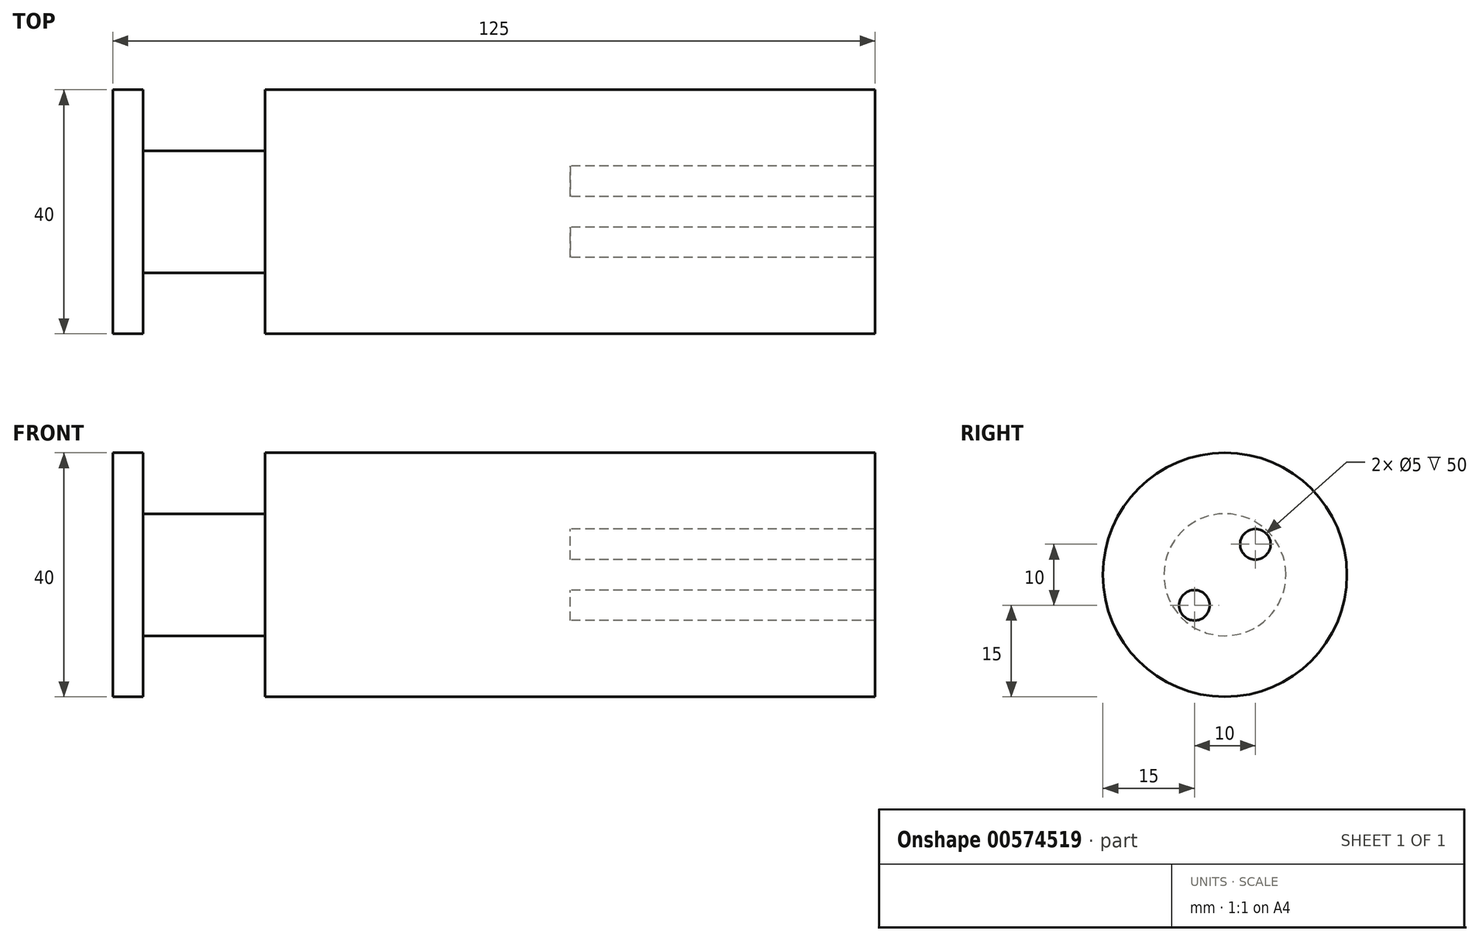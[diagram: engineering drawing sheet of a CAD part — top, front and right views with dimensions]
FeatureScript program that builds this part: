
annotation { "Feature Type Name" : "Feature", "Feature Type Description" : "" }
export const myFeature = defineFeature(function(context is Context, id is Id, definition is map)
    precondition{}
    {
        {
            var Q0;
            Q0=qCreatedBy(makeId("Right.planeOp"),FACE);
            var sketch = newSketch(context, id + "F0", { "sketchPlane" : qUnion([Q0])});
            skCircle(sketch, "E0", {"center": v(0, 0) * mm, "radius": 20 * mm});
            skLineSegment(sketch, "E1", {"start": v(0, 20) * mm, "end": v(0, -20) * mm, "construction": true});
            skLineSegment(sketch, "E2", {"start": v(-20, 0) * mm, "end": v(20, 0) * mm, "construction": true});
            skLineSegment(sketch, "E3.MirrorCS", {"start": v(20, 0) * mm, "end": v(-20, 0) * mm, "construction": true});
            skSolve(sketch);
        }
        {
            var Q0;
            Q0=makeQuery(id+"F0.imprint","IMPRINT",FACE,{"disambiguationData":[TD([[makeQuery(id+"F0.imprint","IMPRINT",EDGE,{"derivedFrom":sQuery(id+"F0.wireOp",EDGE,"E0")}),1.0]])]});
            var Q1;
            Q1=sQuery(id+"F0.wireOp",EDGE,"E0");
            extrude(context, id + "F1", {"entities" : qUnion([Q0]), "surfaceEntities" : qUnion([Q1]), "endBound" : BoundingType.SYMMETRIC, "depth" : 50 * mm, "offsetDistance" : 25 * mm});
        }
        {
            var Q0;
            Q0=makeQuery(id+"F1.opExtrude","CAP_FACE",FACE,{"disambiguationData":[OSD([sQuery(id+"F0.wireOp",EDGE,"E0")])],"isStart":false});
            var sketch = newSketch(context, id + "F2", { "sketchPlane" : qUnion([Q0])});
            skLineSegment(sketch, "E4", {"start": v(0, 20) * mm, "end": v(0, -20) * mm, "construction": true});
            skLineSegment(sketch, "E5", {"start": v(20, 0) * mm, "end": v(-20, 0) * mm, "construction": true});
            skCircle(sketch, "E6", {"center": v(-5, 5) * mm, "radius": 2.5 * mm});
            skCircle(sketch, "E7.MirrorC", {"center": v(5, 5) * mm, "radius": 2.5 * mm});
            skCircle(sketch, "E8.MirrorC", {"center": v(5, -5) * mm, "radius": 2.5 * mm});
            skCircle(sketch, "E9.MirrorC", {"center": v(-5, -5) * mm, "radius": 2.5 * mm});
            skSolve(sketch);
        }
        {
            var Q0;
            Q0=makeQuery(id+"F2.imprint","IMPRINT",FACE,{"disambiguationData":[TD([[makeQuery(id+"F2.imprint","IMPRINT",EDGE,{"derivedFrom":sQuery(id+"F2.wireOp",EDGE,"E6")}),1.0]])]});
            var Q1;
            Q1=makeQuery(id+"F2.imprint","IMPRINT",FACE,{"disambiguationData":[TD([[makeQuery(id+"F2.imprint","IMPRINT",EDGE,{"derivedFrom":sQuery(id+"F2.wireOp",EDGE,"E7.MirrorC")}),-1.0]])]});
            var Q2;
            Q2=makeQuery(id+"F2.imprint","IMPRINT",FACE,{"disambiguationData":[TD([[makeQuery(id+"F2.imprint","IMPRINT",EDGE,{"derivedFrom":sQuery(id+"F2.wireOp",EDGE,"E8.MirrorC")}),1.0]])]});
            var Q3;
            Q3=makeQuery(id+"F2.imprint","IMPRINT",FACE,{"disambiguationData":[TD([[makeQuery(id+"F2.imprint","IMPRINT",EDGE,{"derivedFrom":sQuery(id+"F2.wireOp",EDGE,"E9.MirrorC")}),-1.0]])]});
            extrude(context, id + "F3", {"entities" : qUnion([Q0, Q1, Q2, Q3]), "operationType" : NewBodyOperationType.ADD, "depth" : 50 * mm, "offsetDistance" : 25 * mm});
        }
        {
            var Q0;
            Q0=makeQuery(id+"F1.opExtrude","CAP_FACE",FACE,{"disambiguationData":[OSD([sQuery(id+"F0.wireOp",EDGE,"E0")])],"isStart":true});
            var sketch = newSketch(context, id + "F4", { "sketchPlane" : qUnion([Q0])});
            skCircle(sketch, "E10", {"center": v(0, 0) * mm, "radius": 10 * mm});
            skSolve(sketch);
        }
        {
            var Q0;
            Q0=makeQuery(id+"F4.imprint","IMPRINT",FACE,{"disambiguationData":[TD([[makeQuery(id+"F4.imprint","IMPRINT",EDGE,{"derivedFrom":sQuery(id+"F4.wireOp",EDGE,"E10")}),1.0]])]});
            extrude(context, id + "F5", {"entities" : qUnion([Q0]), "operationType" : NewBodyOperationType.ADD, "depth" : 25 * mm, "offsetDistance" : 25 * mm});
        }
        {
            var Q0;
            Q0=makeQuery(id+"F5.opExtrude","CAP_FACE",FACE,{"disambiguationData":[OSD([sQuery(id+"F4.wireOp",EDGE,"E10")])],"isStart":false});
            var sketch = newSketch(context, id + "F6", { "sketchPlane" : qUnion([Q0])});
            skCircle(sketch, "E11", {"center": v(0, 0) * mm, "radius": 20 * mm});
            skSolve(sketch);
        }
        {
            var Q0;
            Q0=makeQuery(id+"F6.imprint","IMPRINT",FACE,{"disambiguationData":[TD([[makeQuery(id+"F6.imprint","IMPRINT",EDGE,{"derivedFrom":sQuery(id+"F6.wireOp",EDGE,"E11")}),1.0]])]});
            var Q1;
            Q1=sQuery(id+"F6.wireOp",EDGE,"E11");
            extrude(context, id + "F7", {"entities" : qUnion([Q0]), "operationType" : NewBodyOperationType.ADD, "surfaceEntities" : qUnion([Q1]), "oppositeDirection" : true, "depth" : 5 * mm, "offsetDistance" : 25 * mm});
        }
    });
